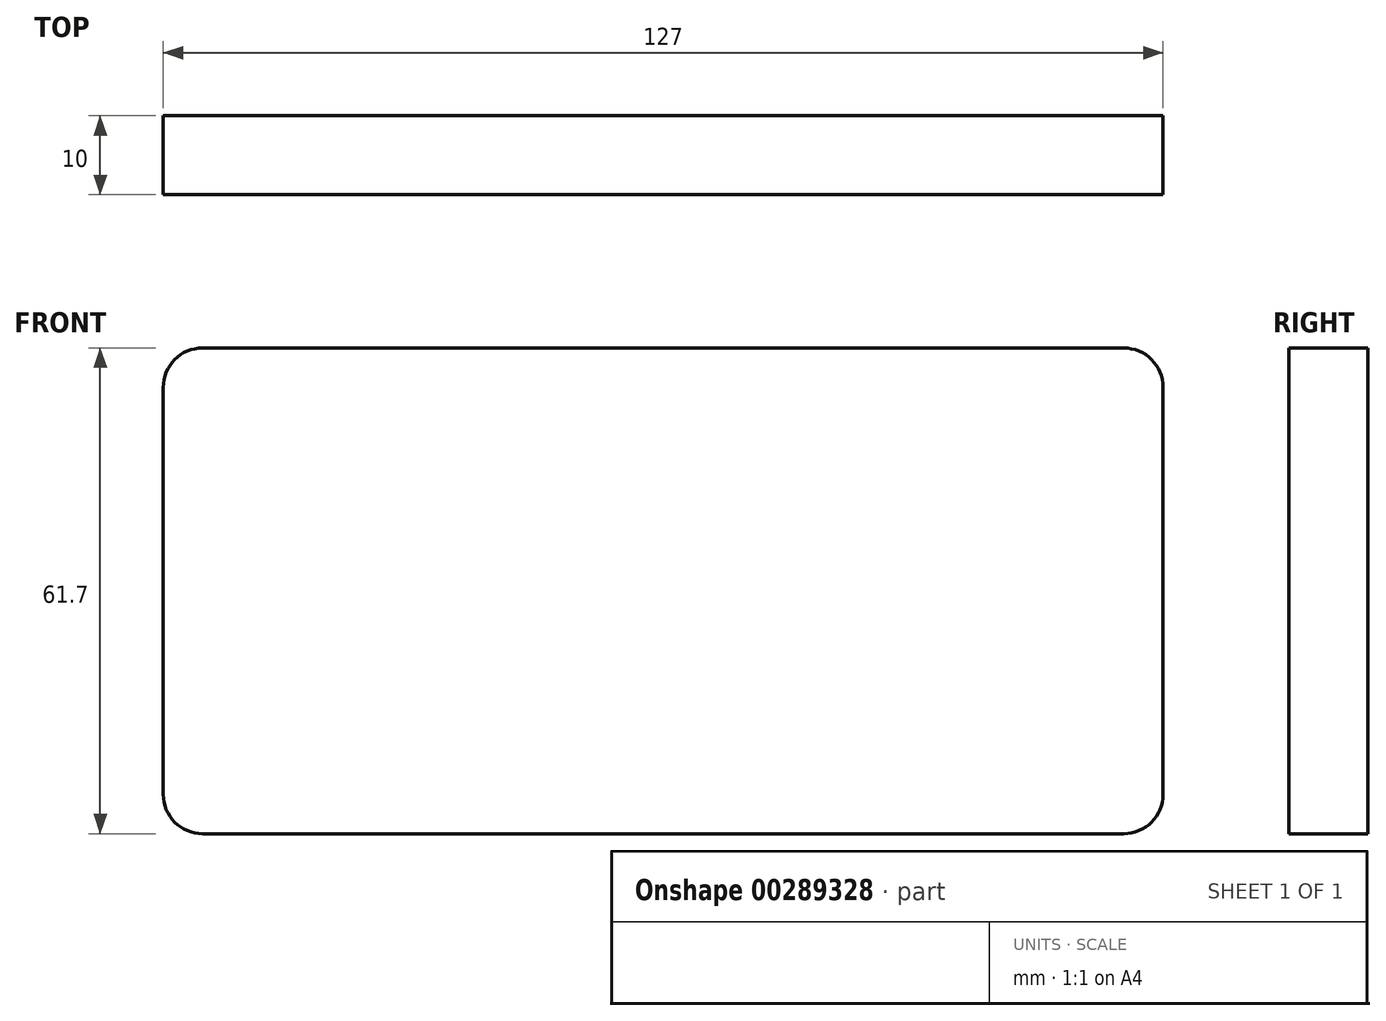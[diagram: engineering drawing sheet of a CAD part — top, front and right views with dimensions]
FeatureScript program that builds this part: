
annotation { "Feature Type Name" : "Feature", "Feature Type Description" : "" }
export const myFeature = defineFeature(function(context is Context, id is Id, definition is map)
    precondition{}
    {
        {
            var Q0;
            Q0=qCreatedBy(makeId("Front.planeOp"),FACE);
            var sketch = newSketch(context, id + "F0", { "sketchPlane" : qUnion([Q0]) });
            skLineSegment(sketch, "E0.bottom", {"start": v(63.5, -30.85) * mm, "end": v(-63.5, -30.85) * mm});
            skLineSegment(sketch, "E0.top", {"start": v(63.5, 30.85) * mm, "end": v(-63.5, 30.85) * mm});
            skLineSegment(sketch, "E0.left", {"start": v(63.5, -30.85) * mm, "end": v(63.5, 30.85) * mm});
            skLineSegment(sketch, "E0.right", {"start": v(-63.5, -30.85) * mm, "end": v(-63.5, 30.85) * mm});
            skPoint(sketch, "E0.middle", {"position": v(0, 0) * mm});
            skSolve(sketch);
        }
        {
            var Q0;
            Q0=makeQuery(id+"F0.imprint","IMPRINT",FACE,{"disambiguationData":[TD([[makeQuery(id+"F0.imprint","IMPRINT",EDGE,{"derivedFrom":sQuery(id+"F0.wireOp",EDGE,"E0.bottom")}),-1.0]])]});
            extrude(context, id + "F1", {"entities" : qUnion([Q0]), "depth" : 10 * mm, "offsetDistance" : 25 * mm});
        }
        {
            var Q0;
            Q0=makeQuery(id+"F1.opExtrude","SWEPT_EDGE",EDGE,{"disambiguationData":[OSD([sQuery(id+"F0.wireOp",EDGE,"E0.top"),sQuery(id+"F0.wireOp",EDGE,"E0.right")])]});
            var Q1;
            Q1=makeQuery(id+"F1.opExtrude","SWEPT_EDGE",EDGE,{"disambiguationData":[OSD([sQuery(id+"F0.wireOp",EDGE,"E0.top"),sQuery(id+"F0.wireOp",EDGE,"E0.left")])]});
            var Q2;
            Q2=makeQuery(id+"F1.opExtrude","SWEPT_EDGE",EDGE,{"disambiguationData":[OSD([sQuery(id+"F0.wireOp",EDGE,"E0.bottom"),sQuery(id+"F0.wireOp",EDGE,"E0.left")])]});
            var Q3;
            Q3=makeQuery(id+"F1.opExtrude","SWEPT_EDGE",EDGE,{"disambiguationData":[OSD([sQuery(id+"F0.wireOp",EDGE,"E0.bottom"),sQuery(id+"F0.wireOp",EDGE,"E0.right")])]});
            fillet(context, id + "F2", {"entities" : qUnion([Q0, Q1, Q2, Q3]), "radius" : 5 * mm, "tangentPropagation" : true});
        }
    });
